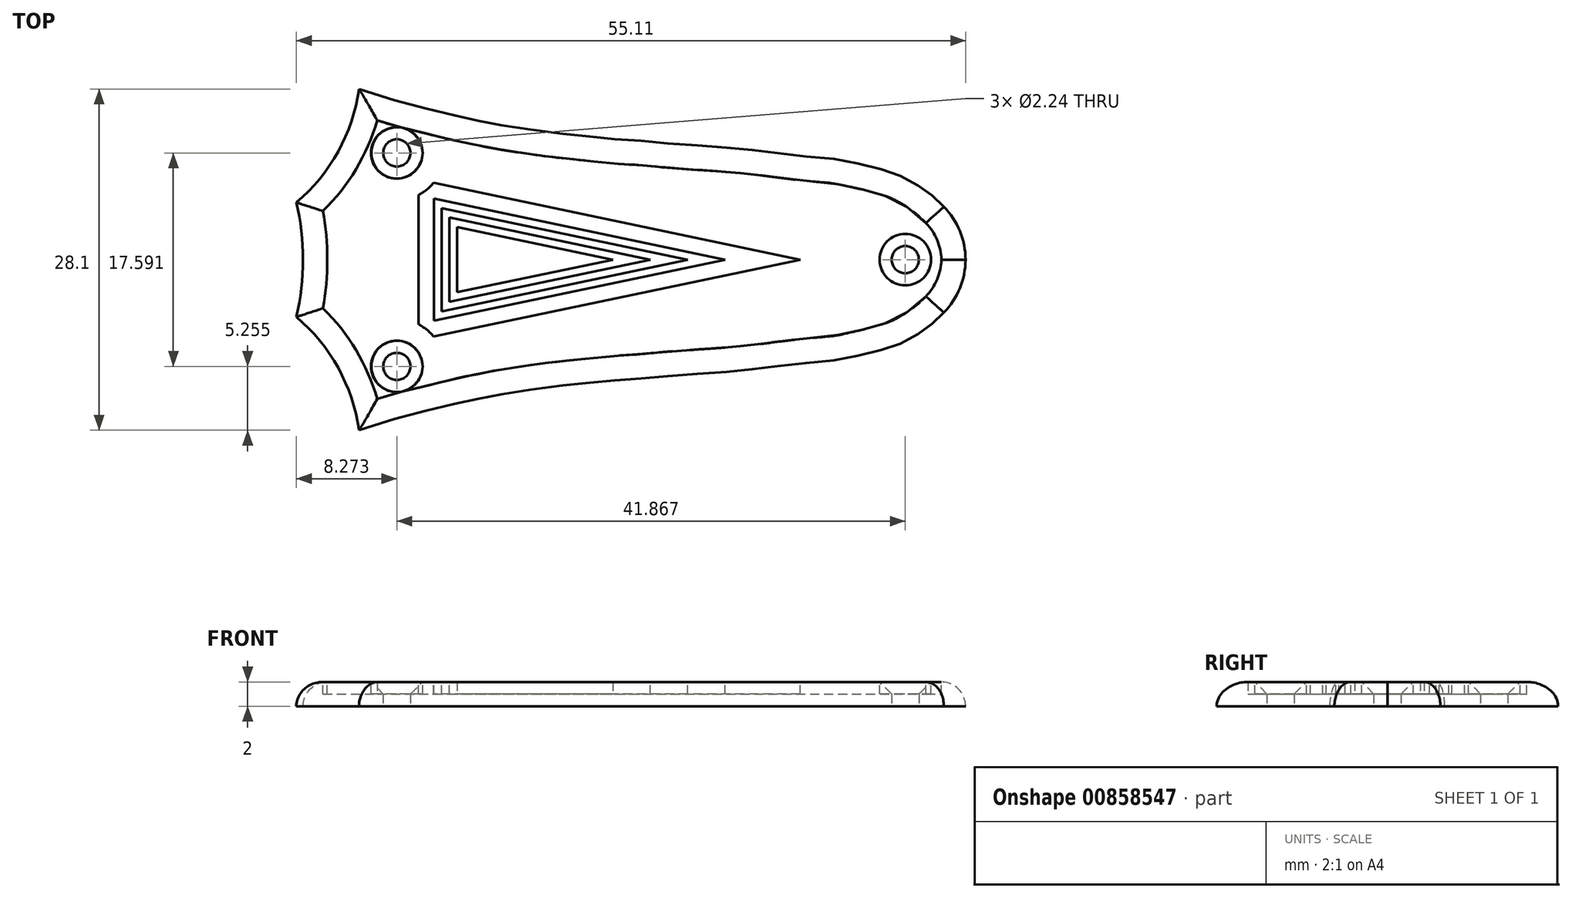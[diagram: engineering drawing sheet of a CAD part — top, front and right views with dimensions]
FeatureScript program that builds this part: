
annotation { "Feature Type Name" : "Feature", "Feature Type Description" : "" }
export const myFeature = defineFeature(function(context is Context, id is Id, definition is map)
    precondition{}
    {
        {
            var Q0;
            Q0=qCreatedBy(makeId("Top.planeOp"),FACE);
            var sketch = newSketch(context, id + "F0", { "sketchPlane" : qUnion([Q0])});
            skLineSegment(sketch, "E0", {"start": v(-62.1, 0) * mm, "end": v(39.32, 0) * mm, "construction": true});
            skArc(sketch, "E1", {"start": v(-29.9, 0) * mm, "mid": v(-30.03, 2.38) * mm, "end": v(-30.44, 4.72) * mm});
            skArc(sketch, "E2", {"start": v(-30.44, 4.72) * mm, "mid": v(-27, 8.91) * mm, "end": v(-25.28, 14.05) * mm});
            skFitSpline(sketch, "E3", {"points": [v(-25.28, 14.05) * mm, v(-21.81, 12.97) * mm, v(-19.3, 12.34) * mm, v(-17.11, 11.8) * mm, v(-15.66, 11.5) * mm, v(-14.19, 11.2) * mm, v(-12.23, 10.87) * mm, v(-9.46, 10.49) * mm, v(-7.16, 10.23) * mm, v(-5.54, 10.07) * mm, v(-3.73, 9.9) * mm, v(-1.9, 9.78) * mm, v(0, 9.6) * mm, v(2.37, 9.42) * mm, v(4.72, 9.26) * mm, v(6.46, 9.1) * mm, v(8.31, 8.9) * mm, v(9.98, 8.68) * mm, v(12.44, 8.42) * mm, v(14.23, 8.24) * mm, v(15.76, 7.92) * mm, v(17.34, 7.55) * mm, v(18.6, 7.17) * mm, v(19.45, 6.85) * mm, v(20.46, 6.3) * mm, v(21.21, 5.83) * mm, v(21.86, 5.32) * mm, v(22.42, 4.86) * mm, v(22.88, 4.37) * mm], "startDerivative": vector(69.45, -22.65) * mm, "endDerivative": vector(19.5, -22.69) * mm});
            skPoint(sketch, "E4", {"position": v(24.67, 0) * mm});
            skArc(sketch, "E5", {"start": v(24.67, 0) * mm, "mid": v(24.19, 2.35) * mm, "end": v(22.88, 4.37) * mm});
            skArc(sketch, "E6.MirrorCS", {"start": v(-29.9, 0) * mm, "mid": v(-30.03, -2.38) * mm, "end": v(-30.44, -4.72) * mm});
            skArc(sketch, "E7.MirrorCS", {"start": v(-30.44, -4.72) * mm, "mid": v(-27, -8.91) * mm, "end": v(-25.28, -14.05) * mm});
            skFitSpline(sketch, "E8.MirrorCS", {"points": [v(-25.28, -14.05) * mm, v(-21.81, -12.97) * mm, v(-19.3, -12.34) * mm, v(-17.11, -11.8) * mm, v(-15.66, -11.5) * mm, v(-14.19, -11.2) * mm, v(-12.23, -10.87) * mm, v(-9.46, -10.49) * mm, v(-7.16, -10.23) * mm, v(-5.54, -10.07) * mm, v(-3.73, -9.9) * mm, v(-1.9, -9.78) * mm, v(0, -9.6) * mm, v(2.37, -9.42) * mm, v(4.72, -9.26) * mm, v(6.46, -9.1) * mm, v(8.31, -8.9) * mm, v(9.98, -8.68) * mm, v(12.44, -8.42) * mm, v(14.23, -8.24) * mm, v(15.76, -7.92) * mm, v(17.34, -7.55) * mm, v(18.6, -7.17) * mm, v(19.45, -6.85) * mm, v(20.46, -6.3) * mm, v(21.21, -5.83) * mm, v(21.86, -5.32) * mm, v(22.42, -4.86) * mm, v(22.88, -4.37) * mm], "startDerivative": vector(69.45, 22.65) * mm, "endDerivative": vector(19.5, 22.69) * mm});
            skArc(sketch, "E9.MirrorCS", {"start": v(24.67, 0) * mm, "mid": v(24.19, -2.35) * mm, "end": v(22.88, -4.37) * mm});
            skCircle(sketch, "E10", {"center": v(-22.17, 8.8) * mm, "radius": 1.12 * mm});
            skCircle(sketch, "E11", {"center": v(19.7, 0) * mm, "radius": 1.12 * mm});
            skCircle(sketch, "E12.MirrorC", {"center": v(-22.17, -8.8) * mm, "radius": 1.12 * mm});
            skSolve(sketch);
        }
        {
            var Q0;
            Q0 = qSketchRegion(id + "F0", true);
            extrude(context, id + "F1", {"entities" : qUnion([Q0]), "depth" : 2 * mm, "offsetDistance" : 25.4 * mm});
        }
        {
            var Q0;
            Q0=makeQuery(id+"F1.opExtrude","CAP_EDGE",EDGE,{"disambiguationData":[OSD([sQuery(id+"F0.wireOp",EDGE,"E1"),sQuery(id+"F0.wireOp",EDGE,"E6.MirrorCS")])],"isStart":false});
            var Q1;
            Q1=makeQuery(id+"F1.opExtrude","CAP_EDGE",EDGE,{"disambiguationData":[OSD([sQuery(id+"F0.wireOp",EDGE,"E7.MirrorCS")])],"isStart":false});
            var Q2;
            Q2=makeQuery(id+"F1.opExtrude","CAP_EDGE",EDGE,{"disambiguationData":[OSD([sQuery(id+"F0.wireOp",EDGE,"E8.MirrorCS")])],"isStart":false});
            var Q3;
            Q3=makeQuery(id+"F1.opExtrude","CAP_EDGE",EDGE,{"disambiguationData":[OSD([sQuery(id+"F0.wireOp",EDGE,"E2")])],"isStart":false});
            var Q4;
            Q4=makeQuery(id+"F1.opExtrude","CAP_EDGE",EDGE,{"disambiguationData":[OSD([sQuery(id+"F0.wireOp",EDGE,"E3")])],"isStart":false});
            var Q5;
            Q5=makeQuery(id+"F1.opExtrude","CAP_EDGE",EDGE,{"disambiguationData":[OSD([sQuery(id+"F0.wireOp",EDGE,"E9.MirrorCS")])],"isStart":false});
            var Q6;
            Q6=makeQuery(id+"F1.opExtrude","CAP_EDGE",EDGE,{"disambiguationData":[OSD([sQuery(id+"F0.wireOp",EDGE,"E5")])],"isStart":false});
            fillet(context, id + "F2", {"entities" : qUnion([Q0, Q1, Q2, Q3, Q4, Q5, Q6]), "radius" : 2 * mm, "tangentPropagation" : true, "allowEdgeOverflow" : false});
        }
        {
            var Q0;
            Q0=makeQuery(id+"F1.opExtrude","CAP_EDGE",EDGE,{"disambiguationData":[OSD([sQuery(id+"F0.wireOp",EDGE,"E10")])],"isStart":false});
            var Q1;
            Q1=makeQuery(id+"F1.opExtrude","CAP_EDGE",EDGE,{"disambiguationData":[OSD([sQuery(id+"F0.wireOp",EDGE,"E12.MirrorC")])],"isStart":false});
            var Q2;
            Q2=makeQuery(id+"F1.opExtrude","CAP_EDGE",EDGE,{"disambiguationData":[OSD([sQuery(id+"F0.wireOp",EDGE,"E11")])],"isStart":false});
            chamfer(context, id + "F3", {"entities" : qUnion([Q0, Q1, Q2]), "width" : 1 * mm, "tangentPropagation" : true});
        }
        {
            var Q0;
            Q0=makeQuery(id+"F1.opExtrude","CAP_FACE",FACE,{"disambiguationData":[OSD([sQuery(id+"F0.wireOp",EDGE,"E1"),sQuery(id+"F0.wireOp",EDGE,"E2"),sQuery(id+"F0.wireOp",EDGE,"E3"),sQuery(id+"F0.wireOp",EDGE,"E5"),sQuery(id+"F0.wireOp",EDGE,"E6.MirrorCS"),sQuery(id+"F0.wireOp",EDGE,"E7.MirrorCS"),sQuery(id+"F0.wireOp",EDGE,"E8.MirrorCS"),sQuery(id+"F0.wireOp",EDGE,"E9.MirrorCS"),sQuery(id+"F0.wireOp",EDGE,"E10"),sQuery(id+"F0.wireOp",EDGE,"E11"),sQuery(id+"F0.wireOp",EDGE,"E12.MirrorC")])],"isStart":false});
            var sketch = newSketch(context, id + "F4", { "sketchPlane" : qUnion([Q0])});
            skPoint(sketch, "E13", {"position": v(19.7, 0) * mm});
            skPoint(sketch, "E14", {"position": v(-22.17, 8.8) * mm});
            skPoint(sketch, "E15", {"position": v(-22.17, -8.8) * mm});
            skLineSegment(sketch, "E16", {"start": v(17.62, 0.44) * mm, "end": v(-20.1, 8.36) * mm, "construction": true});
            skLineSegment(sketch, "E17", {"start": v(-20.1, -8.36) * mm, "end": v(17.62, -0.44) * mm, "construction": true});
            skLineSegment(sketch, "E18", {"start": v(-22.17, 6.67) * mm, "end": v(-22.17, -6.67) * mm, "construction": true});
            skPoint(sketch, "E19", {"position": v(17.62, 0.44) * mm});
            skPoint(sketch, "E20", {"position": v(17.62, -0.44) * mm});
            skArc(sketch, "E21", {"start": v(17.62, 0.44) * mm, "mid": v(17.58, 0) * mm, "end": v(17.62, -0.44) * mm, "construction": true});
            skArc(sketch, "E22", {"start": v(-20.1, 8.36) * mm, "mid": v(-20.83, 7.15) * mm, "end": v(-22.17, 6.67) * mm, "construction": true});
            skArc(sketch, "E23", {"start": v(-22.17, -6.67) * mm, "mid": v(-20.83, -7.15) * mm, "end": v(-20.1, -8.36) * mm, "construction": true});
            skArc(sketch, "E24.0", {"start": v(-19.75, 7.77) * mm, "mid": v(-20.5, 6.75) * mm, "end": v(-21.66, 6.22) * mm});
            skLineSegment(sketch, "E24.1", {"start": v(17.23, 0) * mm, "end": v(-19.75, 7.77) * mm});
            skLineSegment(sketch, "E24.2", {"start": v(-21.66, 6.22) * mm, "end": v(-21.66, -6.22) * mm});
            skArc(sketch, "E24.3", {"start": v(-21.66, -6.22) * mm, "mid": v(-20.5, -6.75) * mm, "end": v(-19.75, -7.77) * mm});
            skLineSegment(sketch, "E24.4", {"start": v(-19.75, -7.77) * mm, "end": v(17.23, 0) * mm});
            skArc(sketch, "E25.0", {"start": v(-19.4, 7.05) * mm, "mid": v(-20.1, 6.26) * mm, "end": v(-21.02, 5.74) * mm});
            skLineSegment(sketch, "E25.1", {"start": v(14.14, 0) * mm, "end": v(-19.4, 7.05) * mm});
            skLineSegment(sketch, "E25.2", {"start": v(-21.02, 5.74) * mm, "end": v(-21.02, -5.74) * mm});
            skArc(sketch, "E25.3", {"start": v(-21.02, -5.74) * mm, "mid": v(-20.1, -6.26) * mm, "end": v(-19.4, -7.05) * mm});
            skLineSegment(sketch, "E25.4", {"start": v(-19.4, -7.05) * mm, "end": v(14.14, 0) * mm});
            skSolve(sketch);
        }
        {
            var Q0;
            Q0=makeQuery(id+"F4.imprint","IMPRINT",FACE,{"disambiguationData":[TD([[makeQuery(id+"F4.imprint","IMPRINT",EDGE,{"derivedFrom":sQuery(id+"F4.wireOp",EDGE,"E24.0")}),1.0]])]});
            extrude(context, id + "F5", {"entities" : qUnion([Q0]), "operationType" : NewBodyOperationType.REMOVE, "oppositeDirection" : true, "depth" : 1 * mm, "offsetDistance" : 25.4 * mm});
        }
        {
            var Q0;
            Q0=makeQuery(id+"F5.boolean.opBoolean","SPLIT",FACE,{"disambiguationData":[TD([makeQuery(id+"F5.opExtrude","SWEPT_FACE",FACE,{"disambiguationData":[OSD([sQuery(id+"F4.wireOp",EDGE,"E25.0")])]})])],"derivedFrom":makeQuery(id+"F1.opExtrude","CAP_FACE",FACE,{"disambiguationData":[OSD([sQuery(id+"F0.wireOp",EDGE,"E1"),sQuery(id+"F0.wireOp",EDGE,"E2"),sQuery(id+"F0.wireOp",EDGE,"E3"),sQuery(id+"F0.wireOp",EDGE,"E5"),sQuery(id+"F0.wireOp",EDGE,"E6.MirrorCS"),sQuery(id+"F0.wireOp",EDGE,"E7.MirrorCS"),sQuery(id+"F0.wireOp",EDGE,"E8.MirrorCS"),sQuery(id+"F0.wireOp",EDGE,"E9.MirrorCS"),sQuery(id+"F0.wireOp",EDGE,"E10"),sQuery(id+"F0.wireOp",EDGE,"E11"),sQuery(id+"F0.wireOp",EDGE,"E12.MirrorC")])],"isStart":false})});
            var sketch = newSketch(context, id + "F6", { "sketchPlane" : qUnion([Q0])});
            skArc(sketch, "E26.0", {"start": v(-19.14, 6.34) * mm, "mid": v(-19.7, 5.77) * mm, "end": v(-20.39, 5.32) * mm});
            skLineSegment(sketch, "E26.1", {"start": v(11.05, 0) * mm, "end": v(-19.14, 6.34) * mm});
            skLineSegment(sketch, "E26.2", {"start": v(-20.39, 5.32) * mm, "end": v(-20.39, -5.32) * mm});
            skArc(sketch, "E26.3", {"start": v(-20.39, -5.32) * mm, "mid": v(-19.7, -5.77) * mm, "end": v(-19.14, -6.34) * mm});
            skLineSegment(sketch, "E26.4", {"start": v(-19.14, -6.34) * mm, "end": v(11.05, 0) * mm});
            skArc(sketch, "E27.0", {"start": v(-18.9, 5.64) * mm, "mid": v(-19.3, 5.27) * mm, "end": v(-19.75, 4.96) * mm});
            skLineSegment(sketch, "E27.1", {"start": v(7.96, 0) * mm, "end": v(-18.9, 5.64) * mm});
            skLineSegment(sketch, "E27.2", {"start": v(-19.75, 4.96) * mm, "end": v(-19.75, -4.96) * mm});
            skArc(sketch, "E27.3", {"start": v(-19.75, -4.96) * mm, "mid": v(-19.3, -5.27) * mm, "end": v(-18.9, -5.64) * mm});
            skLineSegment(sketch, "E27.4", {"start": v(-18.9, -5.64) * mm, "end": v(7.96, 0) * mm});
            skSolve(sketch);
        }
        {
            var Q0;
            Q0=makeQuery(id+"F6.imprint","IMPRINT",FACE,{"disambiguationData":[TD([[makeQuery(id+"F6.imprint","IMPRINT",EDGE,{"derivedFrom":sQuery(id+"F6.wireOp",EDGE,"E26.0")}),1.0]])]});
            extrude(context, id + "F7", {"entities" : qUnion([Q0]), "operationType" : NewBodyOperationType.REMOVE, "oppositeDirection" : true, "depth" : 1 * mm, "offsetDistance" : 25.4 * mm});
        }
        {
            var Q0;
            Q0=makeQuery(id+"F7.boolean.opBoolean","SPLIT",FACE,{"disambiguationData":[TD([makeQuery(id+"F7.opExtrude","SWEPT_FACE",FACE,{"disambiguationData":[OSD([sQuery(id+"F6.wireOp",EDGE,"E27.0")])]})])],"derivedFrom":makeQuery(id+"F5.boolean.opBoolean","SPLIT",FACE,{"disambiguationData":[TD([makeQuery(id+"F5.opExtrude","SWEPT_FACE",FACE,{"disambiguationData":[OSD([sQuery(id+"F4.wireOp",EDGE,"E25.0")])]})])],"derivedFrom":makeQuery(id+"F1.opExtrude","CAP_FACE",FACE,{"disambiguationData":[OSD([sQuery(id+"F0.wireOp",EDGE,"E1"),sQuery(id+"F0.wireOp",EDGE,"E2"),sQuery(id+"F0.wireOp",EDGE,"E3"),sQuery(id+"F0.wireOp",EDGE,"E5"),sQuery(id+"F0.wireOp",EDGE,"E6.MirrorCS"),sQuery(id+"F0.wireOp",EDGE,"E7.MirrorCS"),sQuery(id+"F0.wireOp",EDGE,"E8.MirrorCS"),sQuery(id+"F0.wireOp",EDGE,"E9.MirrorCS"),sQuery(id+"F0.wireOp",EDGE,"E10"),sQuery(id+"F0.wireOp",EDGE,"E11"),sQuery(id+"F0.wireOp",EDGE,"E12.MirrorC")])],"isStart":false})})});
            var sketch = newSketch(context, id + "F8", { "sketchPlane" : qUnion([Q0])});
            skLineSegment(sketch, "E28.0", {"start": v(4.87, 0) * mm, "end": v(-19.12, 5.04) * mm});
            skLineSegment(sketch, "E28.1", {"start": v(-19.12, -5.04) * mm, "end": v(4.87, 0) * mm});
            skLineSegment(sketch, "E28.2", {"start": v(-19.12, 5.04) * mm, "end": v(-19.12, -5.04) * mm});
            skLineSegment(sketch, "E29.0", {"start": v(1.79, 0) * mm, "end": v(-18.48, 4.26) * mm});
            skLineSegment(sketch, "E29.1", {"start": v(-18.48, -4.26) * mm, "end": v(1.79, 0) * mm});
            skLineSegment(sketch, "E29.2", {"start": v(-18.48, 4.26) * mm, "end": v(-18.48, -4.26) * mm});
            skSolve(sketch);
        }
        {
            var Q0;
            Q0=makeQuery(id+"F8.imprint","IMPRINT",FACE,{"disambiguationData":[TD([[makeQuery(id+"F8.imprint","IMPRINT",EDGE,{"derivedFrom":sQuery(id+"F8.wireOp",EDGE,"E28.0")}),1.0]])]});
            extrude(context, id + "F9", {"entities" : qUnion([Q0]), "operationType" : NewBodyOperationType.REMOVE, "oppositeDirection" : true, "depth" : 1 * mm, "offsetDistance" : 25.4 * mm});
        }
        {
            var Q0;
            Q0=makeQuery(id+"F9.boolean.opBoolean","SPLIT",FACE,{"disambiguationData":[TD([makeQuery(id+"F9.opExtrude","SWEPT_FACE",FACE,{"disambiguationData":[OSD([sQuery(id+"F8.wireOp",EDGE,"E29.0")])]})])],"derivedFrom":makeQuery(id+"F7.boolean.opBoolean","SPLIT",FACE,{"disambiguationData":[TD([makeQuery(id+"F7.opExtrude","SWEPT_FACE",FACE,{"disambiguationData":[OSD([sQuery(id+"F6.wireOp",EDGE,"E27.0")])]})])],"derivedFrom":makeQuery(id+"F5.boolean.opBoolean","SPLIT",FACE,{"disambiguationData":[TD([makeQuery(id+"F5.opExtrude","SWEPT_FACE",FACE,{"disambiguationData":[OSD([sQuery(id+"F4.wireOp",EDGE,"E25.0")])]})])],"derivedFrom":makeQuery(id+"F1.opExtrude","CAP_FACE",FACE,{"disambiguationData":[OSD([sQuery(id+"F0.wireOp",EDGE,"E1"),sQuery(id+"F0.wireOp",EDGE,"E2"),sQuery(id+"F0.wireOp",EDGE,"E3"),sQuery(id+"F0.wireOp",EDGE,"E5"),sQuery(id+"F0.wireOp",EDGE,"E6.MirrorCS"),sQuery(id+"F0.wireOp",EDGE,"E7.MirrorCS"),sQuery(id+"F0.wireOp",EDGE,"E8.MirrorCS"),sQuery(id+"F0.wireOp",EDGE,"E9.MirrorCS"),sQuery(id+"F0.wireOp",EDGE,"E10"),sQuery(id+"F0.wireOp",EDGE,"E11"),sQuery(id+"F0.wireOp",EDGE,"E12.MirrorC")])],"isStart":false})})})});
            var sketch = newSketch(context, id + "F10", { "sketchPlane" : qUnion([Q0])});
            skLineSegment(sketch, "E30.0", {"start": v(-1.3, 0) * mm, "end": v(-17.85, 3.48) * mm});
            skLineSegment(sketch, "E30.1", {"start": v(-17.85, -3.48) * mm, "end": v(-1.3, 0) * mm});
            skLineSegment(sketch, "E30.2", {"start": v(-17.85, 3.48) * mm, "end": v(-17.85, -3.48) * mm});
            skSolve(sketch);
        }
        {
            var Q0;
            Q0=makeQuery(id+"F10.imprint","IMPRINT",FACE,{"disambiguationData":[TD([[makeQuery(id+"F10.imprint","IMPRINT",EDGE,{"derivedFrom":sQuery(id+"F10.wireOp",EDGE,"E30.0")}),1.0]])]});
            extrude(context, id + "F11", {"entities" : qUnion([Q0]), "operationType" : NewBodyOperationType.REMOVE, "oppositeDirection" : true, "depth" : 1 * mm, "offsetDistance" : 25.4 * mm});
        }
        {
            var Q0;
            Q0=makeQuery(id+"F11.boolean.opBoolean","COPY",FACE,{"derivedFrom":makeQuery(id+"F11.opExtrude","CAP_FACE",FACE,{"disambiguationData":[OSD([sQuery(id+"F10.wireOp",EDGE,"E30.0"),sQuery(id+"F10.wireOp",EDGE,"E30.1"),sQuery(id+"F10.wireOp",EDGE,"E30.2")])],"isStart":false})});
            var sketch = newSketch(context, id + "F12", { "sketchPlane" : qUnion([Q0])});
            skLineSegment(sketch, "E31.0", {"start": v(-4.4, 0) * mm, "end": v(-17.21, 2.7) * mm});
            skLineSegment(sketch, "E31.1", {"start": v(-17.21, -2.7) * mm, "end": v(-4.4, 0) * mm});
            skLineSegment(sketch, "E31.2", {"start": v(-17.21, 2.7) * mm, "end": v(-17.21, -2.7) * mm});
            skLineSegment(sketch, "E32.0", {"start": v(29.58, 0) * mm, "end": v(-24.2, 11.3) * mm});
            skLineSegment(sketch, "E32.1", {"start": v(-24.2, -11.3) * mm, "end": v(29.58, 0) * mm});
            skLineSegment(sketch, "E32.2", {"start": v(-24.2, 11.3) * mm, "end": v(-24.2, -11.3) * mm});
            skSolve(sketch);
        }
        {
            var Q0;
            Q0=makeQuery(id+"F12.imprint","IMPRINT",FACE,{"disambiguationData":[TD([[makeQuery(id+"F12.imprint","IMPRINT",EDGE,{"derivedFrom":sQuery(id+"F12.wireOp",EDGE,"E31.0")}),1.0]])]});
            extrude(context, id + "F13", {"entities" : qUnion([Q0]), "operationType" : NewBodyOperationType.ADD, "depth" : 1 * mm, "offsetDistance" : 25.4 * mm});
        }
    });
